# Revit family: Edge_TB42_B_Side_Hung_Standard
name_source: partatom
category: Windows
revit_build: Autodesk Revit 2014 (Build: 20130308_1515(x64)
units: mm (PartAtom-declared; Revit-internal decimal feet)

## types (18) — shared parameters
Aluminium Thickness = 1 mm  [stored 0.00328084 ft]
Bead SG Gap = 13 mm
Casement Dimension = 42 mm  [stored 0.137795 ft]
Custom Sash Width = 554 mm  [stored 1.81759 ft]
DG Extrusion Start = 11 mm  [stored 0.0360892 ft]
DG Gasket Finish = Double Glazing Gasket Material
DG Thickness Calc = 4 mm  [stored 0.0131234 ft]
Default Sill Height = 800 mm  [stored 2.62467 ft]
Depth Bead = 28 mm  [stored 0.0918635 ft]
Description = Thermal break casement windows (42mm), Type B side hung
Frame Center Offset = 21 mm  [stored 0.0688976 ft]
Limit Fixed Panel Width Max = 1500 mm
Limit Fixed Panel Width Min = 200 mm  [stored 0.656168 ft]
Limit Sash Height Max = 1500 mm
Limit Sash Height Min = 300 mm  [stored 0.984252 ft]
Limit Sash Width Max = 700 mm  [stored 2.29659 ft]
Limit Sash Width Min = 300 mm  [stored 0.984252 ft]
Limit Window Height Max = 1546 mm
Limit Window Height Min = 346 mm
Limit Window Width Max = 2129 mm
Limit Window Width Min = 829 mm  [stored 2.71982 ft]
Manufacturer = Crealco
Max System DG One Piece Thickness = 6 mm  [stored 0.019685 ft]
Max System DG Unit Thickness = 25 mm  [stored 0.082021 ft]
Model = Edge
Offset Bead SG Center Reversed = 21 mm  [stored 0.0688976 ft]
Offset Mullion Left = 569 mm  [stored 1.8668 ft]
Offset Panel 4 Left = 599 mm  [stored 1.96522 ft]
Offset Sash Left = 23 mm  [stored 0.0754593 ft]
Offset Sash Top = 23 mm  [stored 0.0754593 ft]
Offset Window Exterior = 21 mm  [stored 0.0688976 ft]
SG Gasket Thickness = 6 mm  [stored 0.019685 ft]
Sash Center Offset = 18 mm
Sash Overlap = 7 mm  [stored 0.0229659 ft]
Sash Spacing Inner = 8 mm  [stored 0.0262467 ft]
URL = http://www.crealco.co.za
Wall Closure = By host
Width Bead = 15 mm  [stored 0.0492126 ft]
Width Panel 1 = 539 mm  [stored 1.76837 ft]
Width Profile = 30 mm  [stored 0.0984252 ft]
Width Sash = 524 mm  [stored 1.71916 ft]
Width Sash Opening = 554 mm  [stored 1.81759 ft]
zero-valued in all types: Window Exterior Offset

## per-type parameters (varying)
- EDGE-0909S-1000Pa: Area Pane Left=0.37 m²; Area Pane Right=0.21 m²; Clearvue Insulated LowE SHGC Value=0.431; Clearvue Insulated LowE U Value=2.7; Clearvue Insulated SHGC Value=0.473; Clearvue Insulated U Value=3.14; Clearvue SHGC Value=0.521; Clearvue U Value=5.27; Custom Windload=1000 mm  [stored 3.28084 ft]; Custom Window Height=890 mm  [stored 2.91995 ft]; Custom Window Width=890 mm  [stored 2.91995 ft]; Depth Mullion=0 mm  [stored 0 ft]; Energy Advantage SHGC Value=0.467; Energy Advantage U Value=4.02; Has Stiffener Cap=No; Height=890 mm  [stored 2.91995 ft]; Height Panel 4=830 mm  [stored 2.7231 ft]; Height Sash=814 mm  [stored 2.6706 ft]; Height Sash Opening=844 mm  [stored 2.76903 ft]; Intruderprufe Insulated LowE SHGC Value=0.392; Intruderprufe Insulated LowE U Value=2.66; Intruderprufe Insulated SHGC Value=0.433; Intruderprufe Insulated U Value=3.1; Intruderprufe LowE SHGC Value=0.437; Intruderprufe LowE U Value=4.02; Intruderprufe SHGC Value=0.485; Intruderprufe U Value=5.18; Length Mullion=890 mm  [stored 2.91995 ft]; Max Pane Area=0.37 m²; Mullion Depth Windload Based=0 mm  [stored 0 ft]; Width=890 mm  [stored 2.91995 ft]; Width Panel 4=261 mm  [stored 0.856299 ft]; Windload Design=1000 mm  [stored 3.28084 ft]
- EDGE-1209S-1000Pa: Area Pane Left=0.37 m²; Area Pane Right=0.45 m²; Clearvue Insulated LowE SHGC Value=0.477; Clearvue Insulated LowE U Value=2.56; Clearvue Insulated SHGC Value=0.524; Clearvue Insulated U Value=3.07; Clearvue SHGC Value=0.581; Clearvue U Value=5.38; Custom Windload=1000 mm  [stored 3.28084 ft]; Custom Window Height=890 mm  [stored 2.91995 ft]; Custom Window Width=1190 mm  [stored 3.9042 ft]; Depth Mullion=0 mm  [stored 0 ft]; Energy Advantage SHGC Value=0.52; Energy Advantage U Value=3.97; Has Stiffener Cap=No; Height=890 mm  [stored 2.91995 ft]; Height Panel 4=830 mm  [stored 2.7231 ft]; Height Sash=814 mm  [stored 2.6706 ft]; Height Sash Opening=844 mm  [stored 2.76903 ft]; Intruderprufe Insulated LowE SHGC Value=0.435; Intruderprufe Insulated LowE U Value=2.52; Intruderprufe Insulated SHGC Value=0.481; Intruderprufe Insulated U Value=3.02; Intruderprufe LowE SHGC Value=0.485; Intruderprufe LowE U Value=3.96; Intruderprufe SHGC Value=0.542; Intruderprufe U Value=5.29; Length Mullion=890 mm  [stored 2.91995 ft]; Max Pane Area=0.45 m²; Mullion Depth Windload Based=0 mm  [stored 0 ft]; Width=1190 mm  [stored 3.9042 ft]; Width Panel 4=561 mm; Windload Design=1000 mm  [stored 3.28084 ft]
- EDGE-1509S-1000Pa: Area Pane Left=0.37 m²; Area Pane Right=0.7 m²; Clearvue Insulated LowE SHGC Value=0.504; Clearvue Insulated LowE U Value=2.48; Clearvue Insulated SHGC Value=0.55; Clearvue Insulated U Value=3.02; Clearvue SHGC Value=0.617; Clearvue U Value=5.45; Custom Windload=1000 mm  [stored 3.28084 ft]; Custom Window Height=890 mm  [stored 2.91995 ft]; Custom Window Width=1490 mm  [stored 4.88845 ft]; Depth Mullion=0 mm  [stored 0 ft]; Energy Advantage SHGC Value=0.551; Energy Advantage U Value=3.94; Has Stiffener Cap=No; Height=890 mm  [stored 2.91995 ft]; Height Panel 4=830 mm  [stored 2.7231 ft]; Height Sash=814 mm  [stored 2.6706 ft]; Height Sash Opening=844 mm  [stored 2.76903 ft]; Intruderprufe Insulated LowE SHGC Value=0.46; Intruderprufe Insulated LowE U Value=2.44; Intruderprufe Insulated SHGC Value=0.509; Intruderprufe Insulated U Value=2.98; Intruderprufe LowE SHGC Value=0.514; Intruderprufe LowE U Value=3.92; Intruderprufe SHGC Value=0.575; Intruderprufe U Value=5.35; Length Mullion=890 mm  [stored 2.91995 ft]; Max Pane Area=0.7 m²; Mullion Depth Windload Based=0 mm  [stored 0 ft]; Width=1490 mm  [stored 4.88845 ft]; Width Panel 4=861 mm; Windload Design=1000 mm  [stored 3.28084 ft]
- EDGE-0912S-1000Pa: Area Pane Left=0.52 m²; Area Pane Right=0.28 m²; Clearvue Insulated LowE SHGC Value=0.45; Clearvue Insulated LowE U Value=2.64; Clearvue Insulated SHGC Value=0.495; Clearvue Insulated U Value=3.11; Clearvue SHGC Value=0.547; Clearvue U Value=5.23; Custom Windload=1000 mm  [stored 3.28084 ft]; Custom Window Height=1190 mm  [stored 3.9042 ft]; Custom Window Width=890 mm  [stored 2.91995 ft]; Depth Mullion=0 mm  [stored 0 ft]; Energy Advantage SHGC Value=0.49; Energy Advantage U Value=4; Has Stiffener Cap=No; Height=1190 mm  [stored 3.9042 ft]; Height Panel 4=1130 mm  [stored 3.70735 ft]; Height Sash=1114 mm  [stored 3.65486 ft]; Height Sash Opening=1144 mm  [stored 3.75328 ft]; Intruderprufe Insulated LowE SHGC Value=0.41; Intruderprufe Insulated LowE U Value=2.6; Intruderprufe Insulated SHGC Value=0.453; Intruderprufe Insulated U Value=3.07; Intruderprufe LowE SHGC Value=0.458; Intruderprufe LowE U Value=4; Intruderprufe SHGC Value=0.51; Intruderprufe U Value=5.22; Length Mullion=1190 mm  [stored 3.9042 ft]; Max Pane Area=0.52 m²; Mullion Depth Windload Based=0 mm  [stored 0 ft]; Width=890 mm  [stored 2.91995 ft]; Width Panel 4=261 mm  [stored 0.856299 ft]; Windload Design=1000 mm  [stored 3.28084 ft]
- EDGE-1212S-1000Pa: Area Pane Left=0.52 m²; Area Pane Right=0.62 m²; Clearvue Insulated LowE SHGC Value=0.495; Clearvue Insulated LowE U Value=2.5; Clearvue Insulated SHGC Value=0.545; Clearvue Insulated U Value=3.03; Clearvue SHGC Value=0.606; Clearvue U Value=5.43; Custom Windload=1000 mm  [stored 3.28084 ft]; Custom Window Height=1190 mm  [stored 3.9042 ft]; Custom Window Width=1190 mm  [stored 3.9042 ft]; Depth Mullion=0 mm  [stored 0 ft]; Energy Advantage SHGC Value=0.542; Energy Advantage U Value=3.95; Has Stiffener Cap=No; Height=1190 mm  [stored 3.9042 ft]; Height Panel 4=1130 mm  [stored 3.70735 ft]; Height Sash=1114 mm  [stored 3.65486 ft]; Height Sash Opening=1144 mm  [stored 3.75328 ft]; Intruderprufe Insulated LowE SHGC Value=0.452; Intruderprufe Insulated LowE U Value=2.46; Intruderprufe Insulated SHGC Value=0.5; Intruderprufe Insulated U Value=2.99; Intruderprufe LowE SHGC Value=0.506; Intruderprufe LowE U Value=3.39; Intruderprufe SHGC Value=0.566; Intruderprufe U Value=5.33; Length Mullion=1190 mm  [stored 3.9042 ft]; Max Pane Area=0.62 m²; Mullion Depth Windload Based=0 mm  [stored 0 ft]; Width=1190 mm  [stored 3.9042 ft]; Width Panel 4=561 mm; Windload Design=1000 mm  [stored 3.28084 ft]
- EDGE-1512S-1000Pa: Area Pane Left=0.52 m²; Area Pane Right=0.95 m²; Clearvue Insulated LowE SHGC Value=0.523; Clearvue Insulated LowE U Value=2.42; Clearvue Insulated SHGC Value=0.575; Clearvue Insulated U Value=2.99; Clearvue SHGC Value=0.641; Clearvue U Value=5.5; Custom Windload=1000 mm  [stored 3.28084 ft]; Custom Window Height=1190 mm  [stored 3.9042 ft]; Custom Window Width=1490 mm  [stored 4.88845 ft]; Depth Mullion=0 mm  [stored 0 ft]; Energy Advantage SHGC Value=0.573; Energy Advantage U Value=3.92; Has Stiffener Cap=No; Height=1190 mm  [stored 3.9042 ft]; Height Panel 4=1130 mm  [stored 3.70735 ft]; Height Sash=1114 mm  [stored 3.65486 ft]; Height Sash Opening=1144 mm  [stored 3.75328 ft]; Intruderprufe Insulated LowE SHGC Value=0.477; Intruderprufe Insulated LowE U Value=2.38; Intruderprufe Insulated SHGC Value=0.528; Intruderprufe Insulated U Value=2.95; Intruderprufe LowE SHGC Value=0.534; Intruderprufe LowE U Value=3.89; Intruderprufe SHGC Value=0.599; Intruderprufe U Value=5.4; Length Mullion=1190 mm  [stored 3.9042 ft]; Max Pane Area=0.95 m²; Mullion Depth Windload Based=0 mm  [stored 0 ft]; Width=1490 mm  [stored 4.88845 ft]; Width Panel 4=861 mm; Windload Design=1000 mm  [stored 3.28084 ft]
- EDGE-0909S-1500Pa: Area Pane Left=0.37 m²; Area Pane Right=0.21 m²; Clearvue Insulated LowE SHGC Value=0.431; Clearvue Insulated LowE U Value=2.7; Clearvue Insulated SHGC Value=0.473; Clearvue Insulated U Value=3.14; Clearvue SHGC Value=0.521; Clearvue U Value=5.27; Custom Windload=1500 mm; Custom Window Height=890 mm  [stored 2.91995 ft]; Custom Window Width=890 mm  [stored 2.91995 ft]; Depth Mullion=0 mm  [stored 0 ft]; Energy Advantage SHGC Value=0.467; Energy Advantage U Value=4.02; Has Stiffener Cap=No; Height=890 mm  [stored 2.91995 ft]; Height Panel 4=830 mm  [stored 2.7231 ft]; Height Sash=814 mm  [stored 2.6706 ft]; Height Sash Opening=844 mm  [stored 2.76903 ft]; Intruderprufe Insulated LowE SHGC Value=0.392; Intruderprufe Insulated LowE U Value=2.66; Intruderprufe Insulated SHGC Value=0.433; Intruderprufe Insulated U Value=3.1; Intruderprufe LowE SHGC Value=0.437; Intruderprufe LowE U Value=4.02; Intruderprufe SHGC Value=0.485; Intruderprufe U Value=5.18; Length Mullion=890 mm  [stored 2.91995 ft]; Max Pane Area=0.37 m²; Mullion Depth Windload Based=0 mm  [stored 0 ft]; Width=890 mm  [stored 2.91995 ft]; Width Panel 4=261 mm  [stored 0.856299 ft]; Windload Design=1500 mm
- EDGE-0909S-2000Pa: Area Pane Left=0.37 m²; Area Pane Right=0.21 m²; Clearvue Insulated LowE SHGC Value=0.431; Clearvue Insulated LowE U Value=2.7; Clearvue Insulated SHGC Value=0.473; Clearvue Insulated U Value=3.14; Clearvue SHGC Value=0.521; Clearvue U Value=5.27; Custom Windload=2000 mm; Custom Window Height=890 mm  [stored 2.91995 ft]; Custom Window Width=890 mm  [stored 2.91995 ft]; Depth Mullion=0 mm  [stored 0 ft]; Energy Advantage SHGC Value=0.467; Energy Advantage U Value=4.02; Has Stiffener Cap=No; Height=890 mm  [stored 2.91995 ft]; Height Panel 4=830 mm  [stored 2.7231 ft]; Height Sash=814 mm  [stored 2.6706 ft]; Height Sash Opening=844 mm  [stored 2.76903 ft]; Intruderprufe Insulated LowE SHGC Value=0.392; Intruderprufe Insulated LowE U Value=2.66; Intruderprufe Insulated SHGC Value=0.433; Intruderprufe Insulated U Value=3.1; Intruderprufe LowE SHGC Value=0.437; Intruderprufe LowE U Value=4.02; Intruderprufe SHGC Value=0.485; Intruderprufe U Value=5.18; Length Mullion=890 mm  [stored 2.91995 ft]; Max Pane Area=0.37 m²; Mullion Depth Windload Based=0 mm  [stored 0 ft]; Width=890 mm  [stored 2.91995 ft]; Width Panel 4=261 mm  [stored 0.856299 ft]; Windload Design=2000 mm
- EDGE-1209S-1500Pa: Area Pane Left=0.37 m²; Area Pane Right=0.45 m²; Clearvue Insulated LowE SHGC Value=0.477; Clearvue Insulated LowE U Value=2.56; Clearvue Insulated SHGC Value=0.524; Clearvue Insulated U Value=3.07; Clearvue SHGC Value=0.581; Clearvue U Value=5.38; Custom Windload=1500 mm; Custom Window Height=890 mm  [stored 2.91995 ft]; Custom Window Width=1190 mm  [stored 3.9042 ft]; Depth Mullion=0 mm  [stored 0 ft]; Energy Advantage SHGC Value=0.52; Energy Advantage U Value=3.97; Has Stiffener Cap=No; Height=890 mm  [stored 2.91995 ft]; Height Panel 4=830 mm  [stored 2.7231 ft]; Height Sash=814 mm  [stored 2.6706 ft]; Height Sash Opening=844 mm  [stored 2.76903 ft]; Intruderprufe Insulated LowE SHGC Value=0.435; Intruderprufe Insulated LowE U Value=2.52; Intruderprufe Insulated SHGC Value=0.481; Intruderprufe Insulated U Value=3.02; Intruderprufe LowE SHGC Value=0.485; Intruderprufe LowE U Value=3.96; Intruderprufe SHGC Value=0.542; Intruderprufe U Value=5.29; Length Mullion=890 mm  [stored 2.91995 ft]; Max Pane Area=0.45 m²; Mullion Depth Windload Based=0 mm  [stored 0 ft]; Width=1190 mm  [stored 3.9042 ft]; Width Panel 4=561 mm; Windload Design=1500 mm
- EDGE-1209S-2000Pa: Area Pane Left=0.37 m²; Area Pane Right=0.45 m²; Clearvue Insulated LowE SHGC Value=0.477; Clearvue Insulated LowE U Value=2.56; Clearvue Insulated SHGC Value=0.524; Clearvue Insulated U Value=3.07; Clearvue SHGC Value=0.581; Clearvue U Value=5.38; Custom Windload=2000 mm; Custom Window Height=890 mm  [stored 2.91995 ft]; Custom Window Width=1190 mm  [stored 3.9042 ft]; Depth Mullion=0 mm  [stored 0 ft]; Energy Advantage SHGC Value=0.52; Energy Advantage U Value=3.97; Has Stiffener Cap=No; Height=890 mm  [stored 2.91995 ft]; Height Panel 4=830 mm  [stored 2.7231 ft]; Height Sash=814 mm  [stored 2.6706 ft]; Height Sash Opening=844 mm  [stored 2.76903 ft]; Intruderprufe Insulated LowE SHGC Value=0.435; Intruderprufe Insulated LowE U Value=2.52; Intruderprufe Insulated SHGC Value=0.481; Intruderprufe Insulated U Value=3.02; Intruderprufe LowE SHGC Value=0.485; Intruderprufe LowE U Value=3.96; Intruderprufe SHGC Value=0.542; Intruderprufe U Value=5.29; Length Mullion=890 mm  [stored 2.91995 ft]; Max Pane Area=0.45 m²; Mullion Depth Windload Based=0 mm  [stored 0 ft]; Width=1190 mm  [stored 3.9042 ft]; Width Panel 4=561 mm; Windload Design=2000 mm
- EDGE-1509S-1500Pa: Area Pane Left=0.37 m²; Area Pane Right=0.7 m²; Clearvue Insulated LowE SHGC Value=0.504; Clearvue Insulated LowE U Value=2.48; Clearvue Insulated SHGC Value=0.55; Clearvue Insulated U Value=3.02; Clearvue SHGC Value=0.617; Clearvue U Value=5.45; Custom Windload=1500 mm; Custom Window Height=890 mm  [stored 2.91995 ft]; Custom Window Width=1490 mm  [stored 4.88845 ft]; Depth Mullion=0 mm  [stored 0 ft]; Energy Advantage SHGC Value=0.551; Energy Advantage U Value=3.94; Has Stiffener Cap=No; Height=890 mm  [stored 2.91995 ft]; Height Panel 4=830 mm  [stored 2.7231 ft]; Height Sash=814 mm  [stored 2.6706 ft]; Height Sash Opening=844 mm  [stored 2.76903 ft]; Intruderprufe Insulated LowE SHGC Value=0.46; Intruderprufe Insulated LowE U Value=2.44; Intruderprufe Insulated SHGC Value=0.509; Intruderprufe Insulated U Value=2.98; Intruderprufe LowE SHGC Value=0.514; Intruderprufe LowE U Value=3.92; Intruderprufe SHGC Value=0.575; Intruderprufe U Value=5.35; Length Mullion=890 mm  [stored 2.91995 ft]; Max Pane Area=0.7 m²; Mullion Depth Windload Based=0 mm  [stored 0 ft]; Width=1490 mm  [stored 4.88845 ft]; Width Panel 4=861 mm; Windload Design=1500 mm
- EDGE-1509S-2000Pa: Area Pane Left=0.37 m²; Area Pane Right=0.7 m²; Clearvue Insulated LowE SHGC Value=0.504; Clearvue Insulated LowE U Value=2.48; Clearvue Insulated SHGC Value=0.55; Clearvue Insulated U Value=3.02; Clearvue SHGC Value=0.617; Clearvue U Value=5.45; Custom Windload=2000 mm; Custom Window Height=890 mm  [stored 2.91995 ft]; Custom Window Width=1490 mm  [stored 4.88845 ft]; Depth Mullion=0 mm  [stored 0 ft]; Energy Advantage SHGC Value=0.551; Energy Advantage U Value=3.94; Has Stiffener Cap=No; Height=890 mm  [stored 2.91995 ft]; Height Panel 4=830 mm  [stored 2.7231 ft]; Height Sash=814 mm  [stored 2.6706 ft]; Height Sash Opening=844 mm  [stored 2.76903 ft]; Intruderprufe Insulated LowE SHGC Value=0.46; Intruderprufe Insulated LowE U Value=2.44; Intruderprufe Insulated SHGC Value=0.509; Intruderprufe Insulated U Value=2.98; Intruderprufe LowE SHGC Value=0.514; Intruderprufe LowE U Value=3.92; Intruderprufe SHGC Value=0.575; Intruderprufe U Value=5.35; Length Mullion=890 mm  [stored 2.91995 ft]; Max Pane Area=0.7 m²; Mullion Depth Windload Based=0 mm  [stored 0 ft]; Width=1490 mm  [stored 4.88845 ft]; Width Panel 4=861 mm; Windload Design=2000 mm
- EDGE-0912S-1500Pa: Area Pane Left=0.52 m²; Area Pane Right=0.28 m²; Clearvue Insulated LowE SHGC Value=0.45; Clearvue Insulated LowE U Value=2.64; Clearvue Insulated SHGC Value=0.495; Clearvue Insulated U Value=3.11; Clearvue SHGC Value=0.547; Clearvue U Value=5.23; Custom Windload=1500 mm; Custom Window Height=1190 mm  [stored 3.9042 ft]; Custom Window Width=890 mm  [stored 2.91995 ft]; Depth Mullion=0 mm  [stored 0 ft]; Energy Advantage SHGC Value=0.49; Energy Advantage U Value=4; Has Stiffener Cap=No; Height=1190 mm  [stored 3.9042 ft]; Height Panel 4=1130 mm  [stored 3.70735 ft]; Height Sash=1114 mm  [stored 3.65486 ft]; Height Sash Opening=1144 mm  [stored 3.75328 ft]; Intruderprufe Insulated LowE SHGC Value=0.41; Intruderprufe Insulated LowE U Value=2.6; Intruderprufe Insulated SHGC Value=0.453; Intruderprufe Insulated U Value=3.07; Intruderprufe LowE SHGC Value=0.458; Intruderprufe LowE U Value=4; Intruderprufe SHGC Value=0.51; Intruderprufe U Value=5.22; Length Mullion=1190 mm  [stored 3.9042 ft]; Max Pane Area=0.52 m²; Mullion Depth Windload Based=0 mm  [stored 0 ft]; Width=890 mm  [stored 2.91995 ft]; Width Panel 4=261 mm  [stored 0.856299 ft]; Windload Design=1500 mm
- EDGE-0912S-2000Pa: Area Pane Left=0.52 m²; Area Pane Right=0.28 m²; Clearvue Insulated LowE SHGC Value=0.45; Clearvue Insulated LowE U Value=2.64; Clearvue Insulated SHGC Value=0.495; Clearvue Insulated U Value=3.11; Clearvue SHGC Value=0.547; Clearvue U Value=5.23; Custom Windload=2000 mm; Custom Window Height=1190 mm  [stored 3.9042 ft]; Custom Window Width=890 mm  [stored 2.91995 ft]; Depth Mullion=0 mm  [stored 0 ft]; Energy Advantage SHGC Value=0.49; Energy Advantage U Value=4; Has Stiffener Cap=No; Height=1190 mm  [stored 3.9042 ft]; Height Panel 4=1130 mm  [stored 3.70735 ft]; Height Sash=1114 mm  [stored 3.65486 ft]; Height Sash Opening=1144 mm  [stored 3.75328 ft]; Intruderprufe Insulated LowE SHGC Value=0.41; Intruderprufe Insulated LowE U Value=2.6; Intruderprufe Insulated SHGC Value=0.453; Intruderprufe Insulated U Value=3.07; Intruderprufe LowE SHGC Value=0.458; Intruderprufe LowE U Value=4; Intruderprufe SHGC Value=0.51; Intruderprufe U Value=5.22; Length Mullion=1190 mm  [stored 3.9042 ft]; Max Pane Area=0.52 m²; Mullion Depth Windload Based=0 mm  [stored 0 ft]; Width=890 mm  [stored 2.91995 ft]; Width Panel 4=261 mm  [stored 0.856299 ft]; Windload Design=2000 mm
- EDGE-1212S-1500Pa: Area Pane Left=0.52 m²; Area Pane Right=0.62 m²; Clearvue Insulated LowE SHGC Value=0.495; Clearvue Insulated LowE U Value=2.5; Clearvue Insulated SHGC Value=0.545; Clearvue Insulated U Value=3.03; Clearvue SHGC Value=0.606; Clearvue U Value=5.43; Custom Windload=1500 mm; Custom Window Height=1190 mm  [stored 3.9042 ft]; Custom Window Width=1190 mm  [stored 3.9042 ft]; Depth Mullion=0 mm  [stored 0 ft]; Energy Advantage SHGC Value=0.542; Energy Advantage U Value=3.95; Has Stiffener Cap=No; Height=1190 mm  [stored 3.9042 ft]; Height Panel 4=1130 mm  [stored 3.70735 ft]; Height Sash=1114 mm  [stored 3.65486 ft]; Height Sash Opening=1144 mm  [stored 3.75328 ft]; Intruderprufe Insulated LowE SHGC Value=0.452; Intruderprufe Insulated LowE U Value=2.46; Intruderprufe Insulated SHGC Value=0.5; Intruderprufe Insulated U Value=2.99; Intruderprufe LowE SHGC Value=0.506; Intruderprufe LowE U Value=3.39; Intruderprufe SHGC Value=0.566; Intruderprufe U Value=5.33; Length Mullion=1190 mm  [stored 3.9042 ft]; Max Pane Area=0.62 m²; Mullion Depth Windload Based=0 mm  [stored 0 ft]; Width=1190 mm  [stored 3.9042 ft]; Width Panel 4=561 mm; Windload Design=1500 mm
- EDGE-1212S-2000Pa: Area Pane Left=0.52 m²; Area Pane Right=0.62 m²; Clearvue Insulated LowE SHGC Value=0.548; Clearvue Insulated LowE U Value=2.15; Clearvue Insulated SHGC Value=0.603; Clearvue Insulated U Value=2.69; Clearvue SHGC Value=0.671; Clearvue U Value=4.99; Custom Windload=2000 mm; Custom Window Height=1190 mm  [stored 3.9042 ft]; Custom Window Width=1190 mm  [stored 3.9042 ft]; Depth Mullion=1 mm  [stored 0.00328084 ft]; Energy Advantage SHGC Value=0.6; Energy Advantage U Value=3.5; Has Stiffener Cap=Yes; Height=1190 mm  [stored 3.9042 ft]; Height Panel 4=1130 mm  [stored 3.70735 ft]; Height Sash=1114 mm  [stored 3.65486 ft]; Height Sash Opening=1144 mm  [stored 3.75328 ft]; Intruderprufe Insulated LowE SHGC Value=0.5; Intruderprufe Insulated LowE U Value=2.11; Intruderprufe Insulated SHGC Value=0.554; Intruderprufe Insulated U Value=2.65; Intruderprufe LowE SHGC Value=0.559; Intruderprufe LowE U Value=3.47; Intruderprufe SHGC Value=0.628; Intruderprufe U Value=4.89; Length Mullion=1190 mm  [stored 3.9042 ft]; Max Pane Area=0.62 m²; Mullion Depth Windload Based=1 mm  [stored 0.00328084 ft]; Width=1190 mm  [stored 3.9042 ft]; Width Panel 4=561 mm; Windload Design=2000 mm
- EDGE-1512S-1500Pa: Area Pane Left=0.52 m²; Area Pane Right=0.95 m²; Clearvue Insulated LowE SHGC Value=0.523; Clearvue Insulated LowE U Value=2.42; Clearvue Insulated SHGC Value=0.575; Clearvue Insulated U Value=2.99; Clearvue SHGC Value=0.641; Clearvue U Value=5.5; Custom Windload=1500 mm; Custom Window Height=1190 mm  [stored 3.9042 ft]; Custom Window Width=1490 mm  [stored 4.88845 ft]; Depth Mullion=0 mm  [stored 0 ft]; Energy Advantage SHGC Value=0.573; Energy Advantage U Value=3.92; Has Stiffener Cap=No; Height=1190 mm  [stored 3.9042 ft]; Height Panel 4=1130 mm  [stored 3.70735 ft]; Height Sash=1114 mm  [stored 3.65486 ft]; Height Sash Opening=1144 mm  [stored 3.75328 ft]; Intruderprufe Insulated LowE SHGC Value=0.477; Intruderprufe Insulated LowE U Value=2.38; Intruderprufe Insulated SHGC Value=0.528; Intruderprufe Insulated U Value=2.95; Intruderprufe LowE SHGC Value=0.534; Intruderprufe LowE U Value=3.89; Intruderprufe SHGC Value=0.599; Intruderprufe U Value=5.4; Length Mullion=1190 mm  [stored 3.9042 ft]; Max Pane Area=0.95 m²; Mullion Depth Windload Based=0 mm  [stored 0 ft]; Width=1490 mm  [stored 4.88845 ft]; Width Panel 4=861 mm; Windload Design=1500 mm
- EDGE-1512S-2000Pa: Area Pane Left=0.52 m²; Area Pane Right=0.95 m²; Clearvue Insulated LowE SHGC Value=0.564; Clearvue Insulated LowE U Value=2.14; Clearvue Insulated SHGC Value=0.621; Clearvue Insulated U Value=2.72; Clearvue SHGC Value=0.693; Clearvue U Value=5.15; Custom Windload=2000 mm; Custom Window Height=1190 mm  [stored 3.9042 ft]; Custom Window Width=1490 mm  [stored 4.88845 ft]; Depth Mullion=1 mm  [stored 0.00328084 ft]; Energy Advantage SHGC Value=0.619; Energy Advantage U Value=3.56; Has Stiffener Cap=Yes; Height=1190 mm  [stored 3.9042 ft]; Height Panel 4=1130 mm  [stored 3.70735 ft]; Height Sash=1114 mm  [stored 3.65486 ft]; Height Sash Opening=1144 mm  [stored 3.75328 ft]; Intruderprufe Insulated LowE SHGC Value=0.516; Intruderprufe Insulated LowE U Value=2.1; Intruderprufe Insulated SHGC Value=0.571; Intruderprufe Insulated U Value=2.67; Intruderprufe LowE SHGC Value=0.577; Intruderprufe LowE U Value=3.35; Intruderprufe SHGC Value=0.649; Intruderprufe U Value=5.04; Length Mullion=1190 mm  [stored 3.9042 ft]; Max Pane Area=0.95 m²; Mullion Depth Windload Based=1 mm  [stored 0.00328084 ft]; Width=1490 mm  [stored 4.88845 ft]; Width Panel 4=861 mm; Windload Design=2000 mm

note: [stored X ft] marks values corroborated as IEEE doubles in the binary element streams (Revit-internal decimal feet)

## geometry (parser evidence)
native form markers: Extrusion x1, Sweep x25
no freeform markers — native parametric forms only
